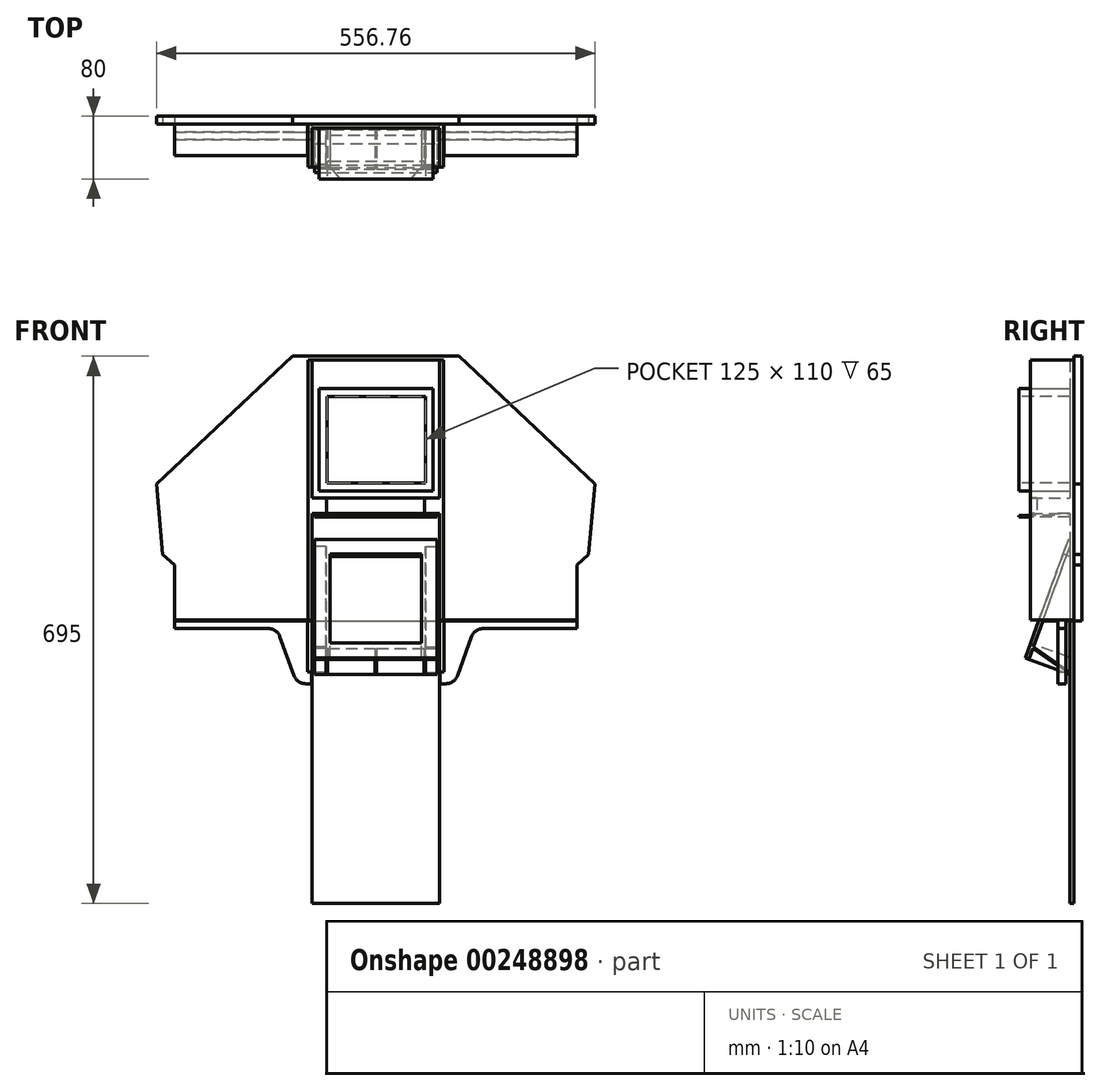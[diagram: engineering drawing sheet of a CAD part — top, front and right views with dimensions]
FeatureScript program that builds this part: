
annotation { "Feature Type Name" : "Feature", "Feature Type Description" : "" }
export const myFeature = defineFeature(function(context is Context, id is Id, definition is map)
    precondition{}
    {
        {
            var Q0;
            Q0=qCreatedBy(makeId("Front.planeOp"),FACE);
            var sketch = newSketch(context, id + "F0", { "sketchPlane" : qUnion([Q0])});
            skLineSegment(sketch, "E0.bottom", {"start": v(0, 0) * mm, "end": v(162, 0) * mm});
            skLineSegment(sketch, "E0.top", {"start": v(0, 20) * mm, "end": v(162, 20) * mm});
            skLineSegment(sketch, "E0.left", {"start": v(0, 0) * mm, "end": v(0, 20) * mm});
            skLineSegment(sketch, "E0.right", {"start": v(162, 0) * mm, "end": v(162, 20) * mm});
            skSolve(sketch);
        }
        {
            var Q0;
            Q0=qSketchRegion(id+"F0",true);
            extrude(context, id + "F1", {"entities" : qUnion([Q0]), "depth" : 50 * mm});
        }
        {
            var Q0;
            Q0=makeQuery(id+"FerxC178B1miYMY_1.boolean.opBoolean","MERGE",FACE,{"derivedFrom":[makeQuery(id+"F1.opExtrude","CAP_FACE",FACE,{"disambiguationData":[OSD([sQuery(id+"F0.wireOp",EDGE,"E0.bottom"),sQuery(id+"F0.wireOp",EDGE,"E0.top"),sQuery(id+"F0.wireOp",EDGE,"E0.left"),sQuery(id+"F0.wireOp",EDGE,"E0.right")])],"isStart":false}),makeQuery(id+"FerxC178B1miYMY_1.opExtrude","SWEPT_FACE",FACE,{"disambiguationData":[OSD([sQuery(id+"FN4QYrKvQ9tnt7i_1.wireOp",EDGE,"MaMVdstS-NuLH-O6Q2-3YOx-SToZS7NwY8gt.top")])]}),makeQuery(id+"FerxC178B1miYMY_1.opExtrude","SWEPT_FACE",FACE,{"disambiguationData":[OSD([sQuery(id+"FN4QYrKvQ9tnt7i_1.wireOp",EDGE,"KNiSyGgG-Fsdb-PpDt-HtjU-rrUHHSUP5IKl.top")])]})]});
            var sketch = newSketch(context, id + "F2", { "sketchPlane" : qUnion([Q0])});
            skLineSegment(sketch, "E1.bottom", {"start": v(18.8, 20) * mm, "end": v(143.2, 20) * mm});
            skLineSegment(sketch, "E1.top", {"start": v(18.8, 0) * mm, "end": v(143.2, 0) * mm});
            skLineSegment(sketch, "E1.left", {"start": v(18.8, 20) * mm, "end": v(18.8, 0) * mm});
            skLineSegment(sketch, "E1.right", {"start": v(143.2, 20) * mm, "end": v(143.2, 0) * mm});
            skSolve(sketch);
        }
        {
            var Q0;
            Q0=qSketchRegion(id+"F2",true);
            extrude(context, id + "F3", {"entities" : qUnion([Q0]), "operationType" : NewBodyOperationType.REMOVE, "oppositeDirection" : true, "depth" : 8 * mm});
        }
        {
            var Q0;
            Q0=makeQuery(id+"F3.boolean.opBoolean","COPY",EDGE,{"derivedFrom":makeQuery(id+"F3.opExtrude","CAP_EDGE",EDGE,{"disambiguationData":[OSD([sQuery(id+"F2.wireOp",EDGE,"E1.left")])],"isStart":false})});
            var Q1;
            Q1=makeQuery(id+"F3.boolean.opBoolean","COPY",EDGE,{"derivedFrom":makeQuery(id+"F3.opExtrude","CAP_EDGE",EDGE,{"disambiguationData":[OSD([sQuery(id+"F2.wireOp",EDGE,"E1.right")])],"isStart":false})});
            fillet(context, id + "F4", {"entities" : qUnion([Q0, Q1]), "radius" : 3 * mm, "tangentPropagation" : true, "allowEdgeOverflow" : false});
        }
        {
            var Q0;
            Q0=makeQuery(id+"F1.opExtrude","SWEPT_FACE",FACE,{"disambiguationData":[OSD([sQuery(id+"F0.wireOp",EDGE,"E0.bottom")])]});
            var sketch = newSketch(context, id + "F5", { "sketchPlane" : qUnion([Q0])});
            skLineSegment(sketch, "E2.bottom", {"start": v(0, 0) * mm, "end": v(162, 0) * mm});
            skLineSegment(sketch, "E2.top", {"start": v(0, -5) * mm, "end": v(162, -5) * mm});
            skLineSegment(sketch, "E2.left", {"start": v(0, 0) * mm, "end": v(0, -5) * mm});
            skLineSegment(sketch, "E2.right", {"start": v(162, 0) * mm, "end": v(162, -5) * mm});
            skSolve(sketch);
        }
        {
            var Q0;
            Q0=qSketchRegion(id+"F5",true);
            extrude(context, id + "F6", {"entities" : qUnion([Q0]), "operationType" : NewBodyOperationType.ADD, "oppositeDirection" : true, "depth" : 195 * mm, "hasSecondDirection" : true, "secondDirectionOppositeDirection" : false, "secondDirectionDepth" : 495 * mm});
        }
        {
            var Q0;
            Q0=makeQuery(id+"F6.opExtrude","SWEPT_FACE",FACE,{"disambiguationData":[OSD([sQuery(id+"F5.wireOp",EDGE,"E2.bottom")])]});
            var sketch = newSketch(context, id + "F7", { "sketchPlane" : qUnion([Q0])});
            skLineSegment(sketch, "E3.bottom", {"start": v(9, 159) * mm, "end": v(154, 159) * mm});
            skLineSegment(sketch, "E3.top", {"start": v(9, 29) * mm, "end": v(154, 29) * mm});
            skLineSegment(sketch, "E3.left", {"start": v(9, 159) * mm, "end": v(9, 29) * mm});
            skLineSegment(sketch, "E3.right", {"start": v(154, 159) * mm, "end": v(154, 29) * mm});
            skSolve(sketch);
        }
        {
            var Q0;
            Q0=qSketchRegion(id+"F7",true);
            extrude(context, id + "F8", {"entities" : qUnion([Q0]), "operationType" : NewBodyOperationType.ADD, "depth" : 65 * mm});
        }
        {
            var Q0;
            Q0=makeQuery(id+"F1.opExtrude","SWEPT_FACE",FACE,{"disambiguationData":[OSD([sQuery(id+"F0.wireOp",EDGE,"E0.bottom")])]});
            var sketch = newSketch(context, id + "F9", { "sketchPlane" : qUnion([Q0])});
            skLineSegment(sketch, "E4.bottom", {"start": v(0, 50) * mm, "end": v(-5, 50) * mm});
            skLineSegment(sketch, "E4.top", {"start": v(0, -5) * mm, "end": v(-5, -5) * mm});
            skLineSegment(sketch, "E4.left", {"start": v(0, 50) * mm, "end": v(0, -5) * mm});
            skLineSegment(sketch, "E4.right", {"start": v(-5, 50) * mm, "end": v(-5, -5) * mm});
            skLineSegment(sketch, "E5.bottom", {"start": v(162, 50) * mm, "end": v(167, 50) * mm});
            skLineSegment(sketch, "E5.top", {"start": v(162, -5) * mm, "end": v(167, -5) * mm});
            skLineSegment(sketch, "E5.left", {"start": v(162, 50) * mm, "end": v(162, -5) * mm});
            skLineSegment(sketch, "E5.right", {"start": v(167, 50) * mm, "end": v(167, -5) * mm});
            skSolve(sketch);
        }
        {
            var Q0;
            Q0=qSketchRegion(id+"F9",true);
            extrude(context, id + "F10", {"entities" : qUnion([Q0]), "operationType" : NewBodyOperationType.ADD, "oppositeDirection" : true, "depth" : 195 * mm, "hasSecondDirection" : true, "secondDirectionOppositeDirection" : false, "secondDirectionDepth" : 135 * mm});
        }
        {
            var Q0;
            Q0=makeQuery(id+"F10.boolean.opBoolean","MERGE",FACE,{"derivedFrom":[makeQuery(id+"F6.opExtrude","SWEPT_FACE",FACE,{"disambiguationData":[OSD([sQuery(id+"F5.wireOp",EDGE,"E2.top")])]}),makeQuery(id+"F10.opExtrude","SWEPT_FACE",FACE,{"disambiguationData":[OSD([sQuery(id+"F9.wireOp",EDGE,"E4.top")])]}),makeQuery(id+"F10.opExtrude","SWEPT_FACE",FACE,{"disambiguationData":[OSD([sQuery(id+"F9.wireOp",EDGE,"E5.top")])]})]});
            var sketch = newSketch(context, id + "F11", { "sketchPlane" : qUnion([Q0])});
            skLineSegment(sketch, "E6", {"start": v(-186.5, 200) * mm, "end": v(24.5, 200) * mm});
            skLineSegment(sketch, "E7", {"start": v(24.5, 200) * mm, "end": v(197.38, 37.88) * mm});
            skLineSegment(sketch, "E8", {"start": v(197.38, 37.88) * mm, "end": v(189.5, -51.77) * mm});
            skLineSegment(sketch, "E9", {"start": v(189.5, -51.77) * mm, "end": v(174.5, -65) * mm});
            skLineSegment(sketch, "E10", {"start": v(174.5, -65) * mm, "end": v(174.5, -136) * mm});
            skLineSegment(sketch, "E11", {"start": v(174.5, -136) * mm, "end": v(-336.5, -136) * mm});
            skLineSegment(sketch, "E12", {"start": v(-336.5, -136) * mm, "end": v(-336.5, -65) * mm});
            skLineSegment(sketch, "E13", {"start": v(-336.5, -65) * mm, "end": v(-351.5, -51.77) * mm});
            skLineSegment(sketch, "E14", {"start": v(-351.5, -51.77) * mm, "end": v(-359.38, 37.88) * mm});
            skLineSegment(sketch, "E15", {"start": v(-359.38, 37.88) * mm, "end": v(-186.5, 200) * mm});
            skLineSegment(sketch, "E16", {"start": v(-336.5, -100.5) * mm, "end": v(-167, -100.5) * mm, "construction": true});
            skLineSegment(sketch, "E17", {"start": v(5, -100.5) * mm, "end": v(174.5, -100.5) * mm, "construction": true});
            skSolve(sketch);
        }
        {
            var Q0;
            Q0=qSketchRegion(id+"F11",true);
            extrude(context, id + "F12", {"entities" : qUnion([Q0]), "operationType" : NewBodyOperationType.ADD, "depth" : 10 * mm});
        }
        {
            var Q0;
            {var subQ2=sQuery(id+"F5.wireOp",EDGE,"E2.bottom");Q0=makeQuery(id+"F6.boolean.opBoolean","SPLIT",FACE,{"disambiguationData":[TD([makeQuery(id+"F1.opExtrude","SWEPT_FACE",FACE,{"disambiguationData":[OSD([sQuery(id+"F0.wireOp",EDGE,"E0.bottom")])]})])],"derivedFrom":makeQuery(id+"F6.opExtrude","SWEPT_FACE",FACE,{"disambiguationData":[OSD([subQ2])]})});}
            var sketch = newSketch(context, id + "F13", { "sketchPlane" : qUnion([Q0])});
            skLineSegment(sketch, "E18.bottom", {"start": v(3, -32.5) * mm, "end": v(159, -32.5) * mm});
            skLineSegment(sketch, "E18.top", {"start": v(3, -252.5) * mm, "end": v(159, -252.5) * mm});
            skLineSegment(sketch, "E18.left", {"start": v(3, -32.5) * mm, "end": v(3, -252.5) * mm});
            skLineSegment(sketch, "E18.right", {"start": v(159, -32.5) * mm, "end": v(159, -252.5) * mm});
            skLineSegment(sketch, "E19", {"start": v(3, -252.5) * mm, "end": v(0, -252.5) * mm, "construction": true});
            skLineSegment(sketch, "E20", {"start": v(159, -252.5) * mm, "end": v(162, -252.5) * mm, "construction": true});
            skSolve(sketch);
        }
        {
            var Q0;
            Q0=qSketchRegion(id+"F13",true);
            extrude(context, id + "F14", {"entities" : qUnion([Q0]), "operationType" : NewBodyOperationType.ADD, "depth" : 150 * mm});
        }
        {
            var Q0;
            Q0=makeQuery(id+"F14.opExtrude","SWEPT_FACE",FACE,{"disambiguationData":[OSD([sQuery(id+"F13.wireOp",EDGE,"E18.right")])]});
            var sketch = newSketch(context, id + "F15", { "sketchPlane" : qUnion([Q0])});
            skLineSegment(sketch, "E21", {"start": v(-2, -32.5) * mm, "end": v(-82.07, -252.5) * mm});
            skLineSegment(sketch, "E22", {"start": v(-82.07, -252.5) * mm, "end": v(-150, -252.5) * mm});
            skLineSegment(sketch, "E23", {"start": v(-150, -252.5) * mm, "end": v(-150, -32.5) * mm});
            skLineSegment(sketch, "E24", {"start": v(-150, -32.5) * mm, "end": v(-2, -32.5) * mm});
            skSolve(sketch);
        }
        {
            var Q0;
            Q0=qSketchRegion(id+"F15",true);
            extrude(context, id + "F16", {"entities" : qUnion([Q0]), "operationType" : NewBodyOperationType.REMOVE, "endBound" : BoundingType.UP_TO_NEXT, "oppositeDirection" : true, "depth" : 25 * mm});
        }
        {
            var Q0;
            Q0=makeQuery(id+"F14.opExtrude","SWEPT_FACE",FACE,{"disambiguationData":[OSD([sQuery(id+"F13.wireOp",EDGE,"E18.right")])]});
            var sketch = newSketch(context, id + "F17", { "sketchPlane" : qUnion([Q0])});
            skLineSegment(sketch, "E25", {"start": v(-56.9, -183.31) * mm, "end": v(0, -204.02) * mm});
            skLineSegment(sketch, "E26", {"start": v(0, -204.02) * mm, "end": v(0, -252.5) * mm});
            skLineSegment(sketch, "E27", {"start": v(0, -252.5) * mm, "end": v(-82.07, -252.5) * mm});
            skLineSegment(sketch, "E28", {"start": v(-82.07, -252.5) * mm, "end": v(-56.9, -183.31) * mm});
            skSolve(sketch);
        }
        {
            var Q0;
            Q0=qSketchRegion(id+"F17",true);
            extrude(context, id + "F18", {"entities" : qUnion([Q0]), "operationType" : NewBodyOperationType.REMOVE, "endBound" : BoundingType.UP_TO_NEXT, "oppositeDirection" : true, "depth" : 25 * mm});
        }
        {
            var Q0;
            Q0=makeQuery(id+"F14.opExtrude","SWEPT_FACE",FACE,{"disambiguationData":[OSD([sQuery(id+"F13.wireOp",EDGE,"E18.right")])]});
            var sketch = newSketch(context, id + "F19", { "sketchPlane" : qUnion([Q0])});
            skLineSegment(sketch, "E29", {"start": v(0, -204.02) * mm, "end": v(-47.06, -170.93) * mm});
            skLineSegment(sketch, "E30", {"start": v(-47.06, -170.93) * mm, "end": v(-52.2, -185.02) * mm});
            skLineSegment(sketch, "E31", {"start": v(-52.2, -185.02) * mm, "end": v(0, -204.02) * mm});
            skSolve(sketch);
        }
        {
            var Q0;
            Q0=qSketchRegion(id+"F19",true);
            extrude(context, id + "F20", {"entities" : qUnion([Q0]), "operationType" : NewBodyOperationType.REMOVE, "oppositeDirection" : true, "depth" : 15 * mm});
        }
        {
            var Q0;
            Q0=makeQuery(id+"F14.opExtrude","SWEPT_FACE",FACE,{"disambiguationData":[OSD([sQuery(id+"F13.wireOp",EDGE,"E18.left")])]});
            var sketch = newSketch(context, id + "F21", { "sketchPlane" : qUnion([Q0])});
            skLineSegment(sketch, "E32", {"start": v(0, -204.02) * mm, "end": v(52.2, -185.02) * mm});
            skLineSegment(sketch, "E33", {"start": v(52.2, -185.02) * mm, "end": v(47.06, -170.93) * mm});
            skLineSegment(sketch, "E34", {"start": v(47.06, -170.93) * mm, "end": v(0, -204.02) * mm});
            skSolve(sketch);
        }
        {
            var Q0;
            Q0=qSketchRegion(id+"F21",true);
            extrude(context, id + "F22", {"entities" : qUnion([Q0]), "operationType" : NewBodyOperationType.REMOVE, "oppositeDirection" : true, "depth" : 15 * mm});
        }
        {
            var Q0;
            Q0=makeQuery(id+"F18.boolean.opBoolean","COPY",FACE,{"derivedFrom":makeQuery(id+"F18.opExtrude","SWEPT_FACE",FACE,{"disambiguationData":[OSD([sQuery(id+"F17.wireOp",EDGE,"E25")])]})});
            var sketch = newSketch(context, id + "F23", { "sketchPlane" : qUnion([Q0])});
            skLineSegment(sketch, "E35.bottom", {"start": v(20, -69.78) * mm, "end": v(80, -69.78) * mm});
            skLineSegment(sketch, "E35.top", {"start": v(20, -14.24) * mm, "end": v(80, -14.24) * mm});
            skLineSegment(sketch, "E35.left", {"start": v(20, -69.78) * mm, "end": v(20, -14.24) * mm});
            skLineSegment(sketch, "E35.right", {"start": v(80, -69.78) * mm, "end": v(80, -14.24) * mm});
            skLineSegment(sketch, "E36.bottom", {"start": v(82, -69.78) * mm, "end": v(142, -69.78) * mm});
            skLineSegment(sketch, "E36.top", {"start": v(82, -14.24) * mm, "end": v(142, -14.24) * mm});
            skLineSegment(sketch, "E36.left", {"start": v(82, -69.78) * mm, "end": v(82, -14.24) * mm});
            skLineSegment(sketch, "E36.right", {"start": v(142, -69.78) * mm, "end": v(142, -14.24) * mm});
            skSolve(sketch);
        }
        {
            var Q0;
            Q0=qSketchRegion(id+"F23",true);
            var Q1;
            Q1=makeQuery(id+"F22.boolean.opBoolean","COPY",FACE,{"derivedFrom":makeQuery(id+"F22.opExtrude","SWEPT_FACE",FACE,{"disambiguationData":[OSD([sQuery(id+"F21.wireOp",EDGE,"E34")])]})});
            extrude(context, id + "F24", {"entities" : qUnion([Q0]), "operationType" : NewBodyOperationType.REMOVE, "endBound" : BoundingType.UP_TO_SURFACE, "oppositeDirection" : true, "endBoundEntityFace" : qUnion([Q1]), "depth" : 25 * mm});
        }
        {
            var Q0;
            Q0=makeQuery(id+"F14.opExtrude","SWEPT_FACE",FACE,{"disambiguationData":[OSD([sQuery(id+"F13.wireOp",EDGE,"E18.right")])]});
            var sketch = newSketch(context, id + "F25", { "sketchPlane" : qUnion([Q0])});
            skLineSegment(sketch, "E37", {"start": v(-46.35, -168.98) * mm, "end": v(0, -41.62) * mm});
            skLineSegment(sketch, "E38", {"start": v(0, -41.62) * mm, "end": v(0, -201.58) * mm});
            skLineSegment(sketch, "E39", {"start": v(0, -201.58) * mm, "end": v(-46.35, -168.98) * mm});
            skSolve(sketch);
        }
        {
            var Q0;
            Q0=qSketchRegion(id+"F25",true);
            extrude(context, id + "F26", {"entities" : qUnion([Q0]), "operationType" : NewBodyOperationType.REMOVE, "oppositeDirection" : true, "depth" : 15 * mm});
        }
        {
            var Q0;
            Q0=makeQuery(id+"F16.boolean.opBoolean","COPY",FACE,{"derivedFrom":makeQuery(id+"F16.opExtrude","SWEPT_FACE",FACE,{"disambiguationData":[OSD([sQuery(id+"F15.wireOp",EDGE,"E21")])]})});
            var sketch = newSketch(context, id + "F27", { "sketchPlane" : qUnion([Q0])});
            skLineSegment(sketch, "E40.bottom", {"start": v(23, -51.22) * mm, "end": v(139, -51.22) * mm});
            skLineSegment(sketch, "E40.top", {"start": v(23, -171.72) * mm, "end": v(139, -171.72) * mm});
            skLineSegment(sketch, "E40.left", {"start": v(23, -51.22) * mm, "end": v(23, -171.72) * mm});
            skLineSegment(sketch, "E40.right", {"start": v(139, -51.22) * mm, "end": v(139, -171.72) * mm});
            skSolve(sketch);
        }
        {
            var Q0;
            Q0=qSketchRegion(id+"F27",true);
            var Q1;
            {var subQ2=sQuery(id+"F5.wireOp",EDGE,"E2.bottom");Q1=makeQuery(id+"F26.boolean.opBoolean","MERGE",FACE,{"derivedFrom":[makeQuery(id+"F18.boolean.opBoolean","MERGE",FACE,{"derivedFrom":[makeQuery(id+"F6.boolean.opBoolean","SPLIT",FACE,{"disambiguationData":[TD([makeQuery(id+"F1.opExtrude","SWEPT_FACE",FACE,{"disambiguationData":[OSD([sQuery(id+"F0.wireOp",EDGE,"E0.bottom")])]})])],"derivedFrom":makeQuery(id+"F6.opExtrude","SWEPT_FACE",FACE,{"disambiguationData":[OSD([subQ2])]})}),makeQuery(id+"F18.opExtrude","SWEPT_FACE",FACE,{"disambiguationData":[OSD([sQuery(id+"F17.wireOp",EDGE,"E26")])]})]}),makeQuery(id+"F26.opExtrude","SWEPT_FACE",FACE,{"disambiguationData":[OSD([sQuery(id+"F25.wireOp",EDGE,"E38")])]})]});}
            extrude(context, id + "F28", {"entities" : qUnion([Q0]), "operationType" : NewBodyOperationType.REMOVE, "endBound" : BoundingType.UP_TO_SURFACE, "oppositeDirection" : true, "endBoundEntityFace" : qUnion([Q1]), "depth" : 25 * mm});
        }
        {
            var Q0;
            Q0=makeQuery(id+"F14.opExtrude","SWEPT_FACE",FACE,{"disambiguationData":[OSD([sQuery(id+"F13.wireOp",EDGE,"E18.left")])]});
            var sketch = newSketch(context, id + "F29", { "sketchPlane" : qUnion([Q0])});
            skLineSegment(sketch, "E41", {"start": v(0, -201.58) * mm, "end": v(46.35, -168.98) * mm});
            skLineSegment(sketch, "E42", {"start": v(46.35, -168.98) * mm, "end": v(0, -41.62) * mm});
            skLineSegment(sketch, "E43", {"start": v(0, -41.62) * mm, "end": v(0, -201.58) * mm});
            skSolve(sketch);
        }
        {
            var Q0;
            Q0=qSketchRegion(id+"F29",true);
            extrude(context, id + "F30", {"entities" : qUnion([Q0]), "operationType" : NewBodyOperationType.REMOVE, "oppositeDirection" : true, "depth" : 15 * mm});
        }
        {
            var Q0;
            Q0=makeQuery(id+"F8.opExtrude","CAP_FACE",FACE,{"disambiguationData":[OSD([sQuery(id+"F7.wireOp",EDGE,"E3.bottom"),sQuery(id+"F7.wireOp",EDGE,"E3.top"),sQuery(id+"F7.wireOp",EDGE,"E3.left"),sQuery(id+"F7.wireOp",EDGE,"E3.right")])],"isStart":false});
            var sketch = newSketch(context, id + "F31", { "sketchPlane" : qUnion([Q0])});
            skLineSegment(sketch, "E44.0", {"start": v(19, 149) * mm, "end": v(19, 39) * mm});
            skLineSegment(sketch, "E44.1", {"start": v(144, 149) * mm, "end": v(19, 149) * mm});
            skLineSegment(sketch, "E44.2", {"start": v(144, 39) * mm, "end": v(144, 149) * mm});
            skLineSegment(sketch, "E44.3", {"start": v(19, 39) * mm, "end": v(144, 39) * mm});
            skSolve(sketch);
        }
        {
            var Q0;
            Q0=qSketchRegion(id+"F31",true);
            var Q1;
            {var subQ2=sQuery(id+"F5.wireOp",EDGE,"E2.bottom");Q1=makeQuery(id+"F6.boolean.opBoolean","SPLIT",FACE,{"disambiguationData":[TD([makeQuery(id+"F1.opExtrude","SWEPT_FACE",FACE,{"disambiguationData":[OSD([sQuery(id+"F0.wireOp",EDGE,"E0.top")])]})])],"derivedFrom":makeQuery(id+"F6.opExtrude","SWEPT_FACE",FACE,{"disambiguationData":[OSD([subQ2])]})});}
            extrude(context, id + "F32", {"entities" : qUnion([Q0]), "operationType" : NewBodyOperationType.REMOVE, "endBound" : BoundingType.UP_TO_SURFACE, "oppositeDirection" : true, "endBoundEntityFace" : qUnion([Q1]), "depth" : 25 * mm});
        }
        {
            var Q0;
            Q0=makeQuery(id+"F1.opExtrude","SWEPT_FACE",FACE,{"disambiguationData":[OSD([sQuery(id+"F0.wireOp",EDGE,"E0.bottom")])]});
            var sketch = newSketch(context, id + "F33", { "sketchPlane" : qUnion([Q0])});
            skLineSegment(sketch, "E45.bottom", {"start": v(3, 0) * mm, "end": v(159, 0) * mm});
            skLineSegment(sketch, "E45.top", {"start": v(3, 20) * mm, "end": v(159, 20) * mm});
            skLineSegment(sketch, "E45.left", {"start": v(3, 0) * mm, "end": v(3, 20) * mm});
            skLineSegment(sketch, "E45.right", {"start": v(159, 0) * mm, "end": v(159, 20) * mm});
            skLineSegment(sketch, "E46", {"start": v(3, 0) * mm, "end": v(0, 0) * mm, "construction": true});
            skLineSegment(sketch, "E47", {"start": v(159, 0) * mm, "end": v(162, 0) * mm, "construction": true});
            skSolve(sketch);
        }
        {
            var Q0;
            Q0=qSketchRegion(id+"F33",true);
            extrude(context, id + "F34", {"entities" : qUnion([Q0]), "operationType" : NewBodyOperationType.ADD, "depth" : 2 * mm});
        }
        {
            var Q0;
            Q0=makeQuery(id+"F34.opExtrude","CAP_FACE",FACE,{"disambiguationData":[OSD([sQuery(id+"F33.wireOp",EDGE,"E45.bottom"),sQuery(id+"F33.wireOp",EDGE,"E45.top"),sQuery(id+"F33.wireOp",EDGE,"E45.left"),sQuery(id+"F33.wireOp",EDGE,"E45.right")])],"isStart":false});
            var sketch = newSketch(context, id + "F35", { "sketchPlane" : qUnion([Q0])});
            skLineSegment(sketch, "E48", {"start": v(3, 0) * mm, "end": v(3, 50) * mm});
            skLineSegment(sketch, "E49", {"start": v(3, 50) * mm, "end": v(18.36, 50) * mm});
            skLineSegment(sketch, "E50", {"start": v(26, 53.54) * mm, "end": v(35.68, 65) * mm});
            skLineSegment(sketch, "E51", {"start": v(35.68, 65) * mm, "end": v(125.68, 65) * mm});
            skLineSegment(sketch, "E52", {"start": v(125.68, 65) * mm, "end": v(135.36, 53.54) * mm});
            skLineSegment(sketch, "E53", {"start": v(143, 50) * mm, "end": v(159, 50) * mm});
            skLineSegment(sketch, "E54", {"start": v(159, 50) * mm, "end": v(159, 0) * mm});
            skLineSegment(sketch, "E55", {"start": v(159, 0) * mm, "end": v(3, 0) * mm});
            skPoint(sketch, "E56.visualSharp", {"position": v(23, 50) * mm});
            skArc(sketch, "E56.filletArc", {"start": v(18.36, 50) * mm, "mid": v(22.57, 50.93) * mm, "end": v(26, 53.54) * mm});
            skPoint(sketch, "E57.visualSharp", {"position": v(138.36, 50) * mm});
            skArc(sketch, "E57.filletArc", {"start": v(135.36, 53.54) * mm, "mid": v(138.8, 50.93) * mm, "end": v(143, 50) * mm});
            skLineSegment(sketch, "E58", {"start": v(3, 0) * mm, "end": v(0, 0) * mm, "construction": true});
            skLineSegment(sketch, "E59", {"start": v(159, 0) * mm, "end": v(162, 0) * mm, "construction": true});
            skSolve(sketch);
        }
        {
            var Q0;
            Q0=qSketchRegion(id+"F35",true);
            extrude(context, id + "F36", {"entities" : qUnion([Q0]), "operationType" : NewBodyOperationType.ADD, "depth" : 2 * mm});
        }
        {
            var Q0;
            Q0=makeQuery(id+"F12.opExtrude","CAP_FACE",FACE,{"disambiguationData":[OSD([sQuery(id+"F11.wireOp",EDGE,"E6"),sQuery(id+"F11.wireOp",EDGE,"E7"),sQuery(id+"F11.wireOp",EDGE,"E8"),sQuery(id+"F11.wireOp",EDGE,"E9"),sQuery(id+"F11.wireOp",EDGE,"E10"),sQuery(id+"F11.wireOp",EDGE,"E11"),sQuery(id+"F11.wireOp",EDGE,"E12"),sQuery(id+"F11.wireOp",EDGE,"E13"),sQuery(id+"F11.wireOp",EDGE,"E14"),sQuery(id+"F11.wireOp",EDGE,"E15")])],"isStart":true});
            var sketch = newSketch(context, id + "F37", { "sketchPlane" : qUnion([Q0])});
            skLineSegment(sketch, "E60.bottom", {"start": v(336.5, -136) * mm, "end": v(167.5, -136) * mm});
            skLineSegment(sketch, "E60.top", {"start": v(336.5, -135) * mm, "end": v(167.5, -135) * mm});
            skLineSegment(sketch, "E60.left", {"start": v(336.5, -136) * mm, "end": v(336.5, -135) * mm});
            skLineSegment(sketch, "E60.right", {"start": v(167.5, -136) * mm, "end": v(167.5, -135) * mm});
            skLineSegment(sketch, "E61.bottom", {"start": v(-174.5, -136) * mm, "end": v(-5.5, -136) * mm});
            skLineSegment(sketch, "E61.top", {"start": v(-174.5, -135) * mm, "end": v(-5.5, -135) * mm});
            skLineSegment(sketch, "E61.left", {"start": v(-174.5, -136) * mm, "end": v(-174.5, -135) * mm});
            skLineSegment(sketch, "E61.right", {"start": v(-5.5, -136) * mm, "end": v(-5.5, -135) * mm});
            skSolve(sketch);
        }
        {
            var Q0;
            Q0=qSketchRegion(id+"F37",true);
            extrude(context, id + "F38", {"entities" : qUnion([Q0]), "operationType" : NewBodyOperationType.ADD, "depth" : 40 * mm});
        }
        {
            var Q0;
            {var subQ2=sQuery(id+"F5.wireOp",EDGE,"E2.bottom");Q0=makeQuery(id+"F30.boolean.opBoolean","MERGE",FACE,{"derivedFrom":[makeQuery(id+"F26.boolean.opBoolean","MERGE",FACE,{"derivedFrom":[makeQuery(id+"F18.boolean.opBoolean","MERGE",FACE,{"derivedFrom":[makeQuery(id+"F6.boolean.opBoolean","SPLIT",FACE,{"disambiguationData":[TD([makeQuery(id+"F1.opExtrude","SWEPT_FACE",FACE,{"disambiguationData":[OSD([sQuery(id+"F0.wireOp",EDGE,"E0.bottom")])]})])],"derivedFrom":makeQuery(id+"F6.opExtrude","SWEPT_FACE",FACE,{"disambiguationData":[OSD([subQ2])]})}),makeQuery(id+"F18.opExtrude","SWEPT_FACE",FACE,{"disambiguationData":[OSD([sQuery(id+"F17.wireOp",EDGE,"E26")])]})]}),makeQuery(id+"F26.opExtrude","SWEPT_FACE",FACE,{"disambiguationData":[OSD([sQuery(id+"F25.wireOp",EDGE,"E38")])]})]}),makeQuery(id+"F30.opExtrude","SWEPT_FACE",FACE,{"disambiguationData":[OSD([sQuery(id+"F29.wireOp",EDGE,"E43")])]})]});}
            cPlane(context, id + "F39", {"entities" : qUnion([Q0]), "cplaneType" : CPlaneType.OFFSET, "offset" : 5 * mm, "width" : 150 * mm, "height" : 150 * mm});
        }
        {
            var Q0;
            Q0=qCreatedBy(id+"F39.planeOp",FACE);
            var sketch = newSketch(context, id + "F40", { "sketchPlane" : qUnion([Q0])});
            skLineSegment(sketch, "E62", {"start": v(336.5, -136) * mm, "end": v(167.5, -136) * mm});
            skLineSegment(sketch, "E63", {"start": v(167.5, -136) * mm, "end": v(167.5, -201) * mm});
            skLineSegment(sketch, "E64", {"start": v(167.5, -201) * mm, "end": v(162.5, -201) * mm});
            skLineSegment(sketch, "E65", {"start": v(162.5, -201) * mm, "end": v(162.5, -216) * mm});
            skLineSegment(sketch, "E66", {"start": v(162.5, -216) * mm, "end": v(170.52, -216) * mm});
            skLineSegment(sketch, "E67", {"start": v(184.61, -206.13) * mm, "end": v(202.9, -155.87) * mm});
            skLineSegment(sketch, "E68", {"start": v(217, -146) * mm, "end": v(336.5, -146) * mm});
            skLineSegment(sketch, "E69", {"start": v(336.5, -146) * mm, "end": v(336.5, -136) * mm});
            skPoint(sketch, "E70.visualSharp", {"position": v(181.02, -216) * mm});
            skArc(sketch, "E70.filletArc", {"start": v(170.52, -216) * mm, "mid": v(179.12, -213.29) * mm, "end": v(184.61, -206.13) * mm});
            skPoint(sketch, "E71.visualSharp", {"position": v(206.5, -146) * mm});
            skArc(sketch, "E71.filletArc", {"start": v(217, -146) * mm, "mid": v(208.4, -148.71) * mm, "end": v(202.9, -155.87) * mm});
            skLineSegment(sketch, "E72", {"start": v(-174.5, -136) * mm, "end": v(-5.5, -136) * mm});
            skLineSegment(sketch, "E73", {"start": v(-5.5, -136) * mm, "end": v(-5.5, -201) * mm});
            skLineSegment(sketch, "E74", {"start": v(-5.5, -201) * mm, "end": v(-0.5, -201) * mm});
            skLineSegment(sketch, "E75", {"start": v(-0.5, -201) * mm, "end": v(-0.5, -216) * mm});
            skLineSegment(sketch, "E76", {"start": v(-0.5, -216) * mm, "end": v(-8.52, -216) * mm});
            skLineSegment(sketch, "E77", {"start": v(-22.61, -206.13) * mm, "end": v(-40.9, -155.87) * mm});
            skLineSegment(sketch, "E78", {"start": v(-55, -146) * mm, "end": v(-174.5, -146) * mm});
            skLineSegment(sketch, "E79", {"start": v(-174.5, -146) * mm, "end": v(-174.5, -136) * mm});
            skPoint(sketch, "E80.visualSharp", {"position": v(-19.02, -216) * mm});
            skArc(sketch, "E80.filletArc", {"start": v(-22.61, -206.13) * mm, "mid": v(-17.12, -213.29) * mm, "end": v(-8.52, -216) * mm});
            skPoint(sketch, "E81.visualSharp", {"position": v(-44.5, -146) * mm});
            skArc(sketch, "E81.filletArc", {"start": v(-40.9, -155.87) * mm, "mid": v(-46.4, -148.71) * mm, "end": v(-55, -146) * mm});
            skSolve(sketch);
        }
        {
            var Q0;
            Q0=qSketchRegion(id+"F40",true);
            extrude(context, id + "F41", {"entities" : qUnion([Q0]), "operationType" : NewBodyOperationType.ADD, "depth" : 10 * mm});
        }
    });
